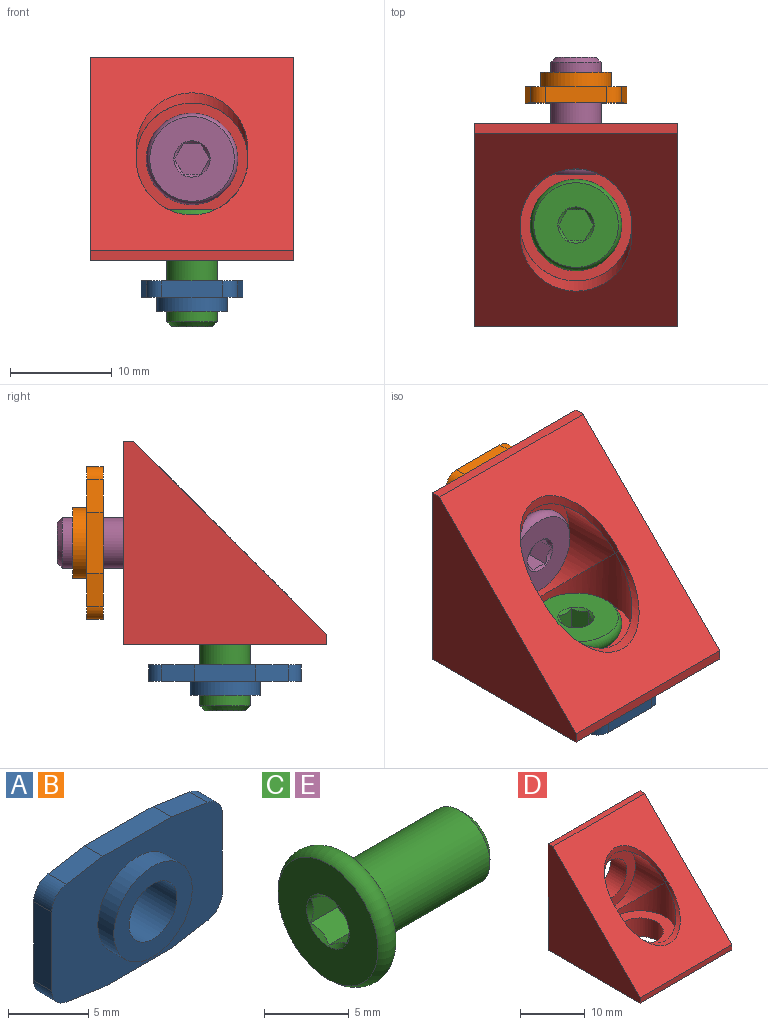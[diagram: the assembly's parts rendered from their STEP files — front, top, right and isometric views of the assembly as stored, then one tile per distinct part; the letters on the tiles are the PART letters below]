
ASSEMBLY  parts=5 mates=4
PART A: 17 faces, bbox 15x3x10 mm
  f0: cylinder r=2.1mm len=4.2mm, axis (0,-1,0), area 39.6mm2, adj f15,f16
  f1: cylinder r=3.45mm len=6.9mm, axis (0,1,0), area 30.3mm2, adj f2,f16
  f2: plane 15x10mm, normal (0,-1,0), area 104.8mm2, adj f1,f3,f4,f5,f6,f7,f8,f9
  f3: cylinder r=1.5mm len=1.6mm, axis (0,1,0), area 3.4mm2, adj f2,f4,f14,f15
  f4: plane 3.24x1.6mm, normal (0.16,0,0.99), area 5.2mm2, adj f2,f3,f5,f15
  f5: plane 6x1.6mm, normal (0,0,1), area 9.6mm2, adj f2,f4,f6,f15
  f6: plane 3.24x1.6mm, normal (-0.16,0,0.99), area 5.2mm2, adj f2,f5,f7,f15
  f7: cylinder r=1.5mm len=1.6mm, axis (0,1,0), area 3.4mm2, adj f2,f6,f8,f15
  f8: plane 6x1.6mm, normal (-1,0,0), area 9.6mm2, adj f2,f7,f9,f15
  f9: cylinder r=1.5mm len=1.6mm, axis (0,1,0), area 3.4mm2, adj f2,f8,f10,f15
  f10: plane 3.24x1.6mm, normal (-0.16,0,-0.99), area 5.2mm2, adj f2,f9,f11,f15
  f11: plane 6x1.6mm, normal (0,0,-1), area 9.6mm2, adj f2,f10,f12,f15
  f12: plane 3.24x1.6mm, normal (0.16,0,-0.99), area 5.2mm2, adj f2,f11,f13,f15
  f13: cylinder r=1.5mm len=1.6mm, axis (0,1,0), area 3.4mm2, adj f2,f12,f14,f15
  f14: plane 6x1.6mm, normal (1,0,0), area 9.6mm2, adj f2,f3,f13,f15
  f15: plane 15x10mm, normal (0,1,0), area 128.3mm2, adj f0,f3,f4,f5,f6,f7,f8,f9
  f16: plane 6.9x6.9mm, normal (0,-1,0), area 23.5mm2, adj f0,f1
PART B: same geometry as A
PART C: 14 faces, bbox 11.8x9.7x9.7 mm
  f0: cone r=1.78mm half-angle=45deg, axis (-1,0,0), area 3.1mm2, adj f5,f8,f9,f10,f11,f12,f13
  f1: torus R=3.5mm, axis (1,0,0), area 46.7mm2, adj f5,f6
  f2: cone r=2mm half-angle=45deg, axis (-1,0,0), area 10mm2, adj f3,f4
  f3: cylinder r=2.5mm len=9.5mm, axis (1,0,0), area 149.2mm2, adj f2,f6
  f4: plane 4x4mm, normal (1,0,0), area 12.6mm2, adj f2
  f5: plane 8.32x8.32mm, normal (-1,0,0), area 44.4mm2, adj f0,f1
  f6: plane 8.32x8.32mm, normal (1,0,0), area 34.8mm2, adj f1,f3
  f7: plane 3.46x3mm, normal (-1,0,0), area 7.8mm2, adj f8,f9,f10,f11,f12,f13
  f8: plane 2.25x1.5mm, normal (0,-0.5,-0.87), area 3.6mm2, adj f0,f7,f9,f13
  f9: plane 2.25x1.73mm, normal (0,-1,0), area 3.6mm2, adj f0,f7,f8,f10
  f10: plane 2.25x1.5mm, normal (0,-0.5,0.87), area 3.6mm2, adj f0,f7,f9,f11
  f11: plane 2.25x1.5mm, normal (0,0.5,0.87), area 3.6mm2, adj f0,f7,f10,f12
  f12: plane 2.25x1.73mm, normal (0,1,0), area 3.6mm2, adj f0,f7,f11,f13
  f13: plane 2.25x1.5mm, normal (0,0.5,-0.87), area 3.6mm2, adj f0,f7,f8,f12
PART D: 15 faces, bbox 20x20x20 mm
  f0: cylinder r=5.5mm len=11mm, axis (0,0,1), area 17.8mm2, adj f2,f5,f14
  f1: cylinder r=5.5mm len=11mm, axis (0,0,1), area 103.6mm2, adj f2,f5,f13
  f2: cylinder r=5.5mm len=11mm, axis (0,-1,0), area 103.6mm2, adj f0,f1,f12
  f3: cylinder r=3.6mm len=7.2mm, axis (0,1,0), area 79.2mm2, adj f7,f12
  f4: cylinder r=3.6mm len=7.2mm, axis (0,0,1), area 79.2mm2, adj f9,f13
  f5: cylinder r=5.5mm len=11mm, axis (0,-1,0), area 17.8mm2, adj f0,f1,f14
  f6: plane 20x1mm, normal (0,-1,0), area 20mm2, adj f8,f9,f10,f14
  f7: plane 20x20mm, normal (0,1,0), area 359.3mm2, adj f3,f8,f9,f10,f11
  f8: plane 20x20mm, normal (-1,0,0), area 219.5mm2, adj f6,f7,f9,f11,f14
  f9: plane 20x20mm, normal (0,0,-1), area 359.3mm2, adj f4,f6,f7,f8,f10
  f10: plane 20x20mm, normal (1,0,0), area 219.5mm2, adj f6,f7,f9,f11,f14
  f11: plane 20x1mm, normal (0,0,1), area 20mm2, adj f7,f8,f10,f14
  f12: plane 11x11mm, normal (0,-1,0), area 54.3mm2, adj f2,f3
  f13: plane 11x11mm, normal (0,0,1), area 54.3mm2, adj f1,f4
  f14: plane 20x19mm, normal (0,-0.71,0.71), area 387.5mm2, adj f0,f5,f6,f8,f10,f11
PART E: same geometry as C
PLACE A rot(axis=(0.58,-0.58,-0.58),120deg) t=(0,0,-12)mm
PLACE B rot(axis=(0.71,0,-0.71),180deg) t=(0,12,0)mm
PLACE C rot(axis=(0,1,0),90deg) t=(0,0,-14.5)mm
PLACE D at identity fixed
PLACE E rot(axis=(0.58,0.58,0.58),120deg) t=(0,14.5,0)mm
MATE fastened C.f0 <-> D.f0  axis (0,0,-1) through (0,0,-6.5)mm
MATE fastened B.f0 <-> D.f2  axis (0,1,0) through (0,15,0)mm
MATE fastened A.f0 <-> D.f4  axis (0,0,-1) through (0,0,-15)mm
MATE fastened E.f0 <-> D.f2  axis (0,1,0) through (0,6.5,0)mm
